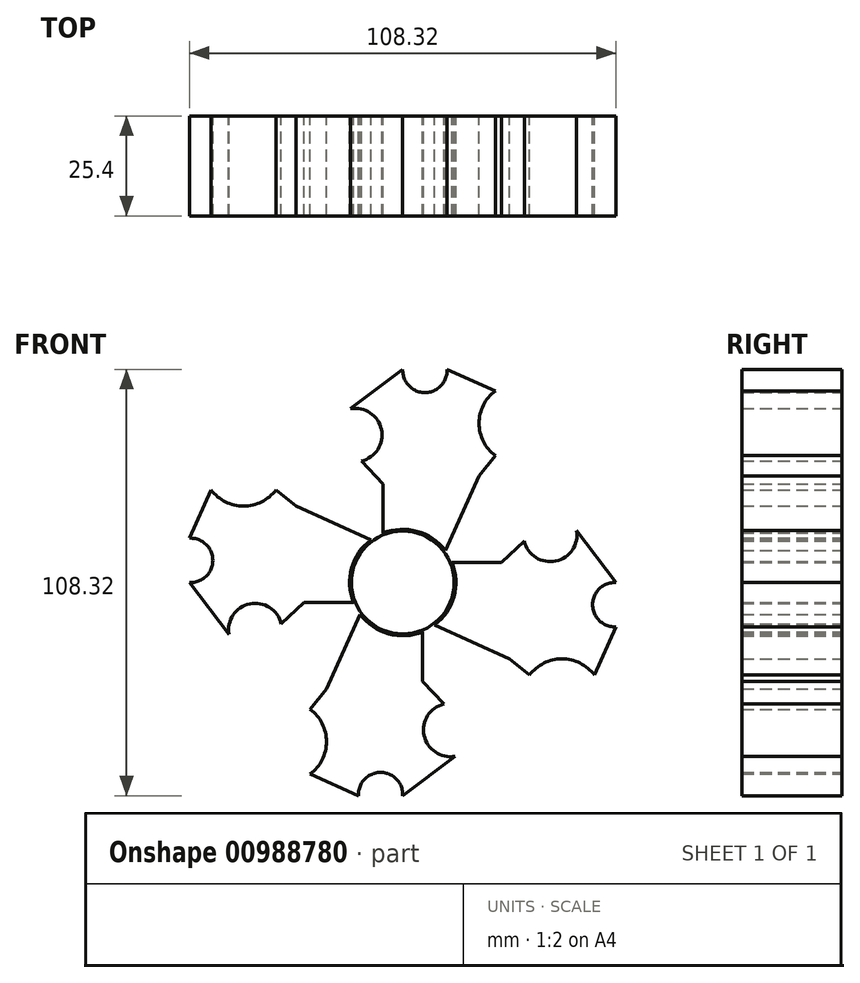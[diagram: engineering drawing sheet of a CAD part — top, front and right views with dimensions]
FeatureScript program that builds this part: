
annotation { "Feature Type Name" : "Feature", "Feature Type Description" : "" }
export const myFeature = defineFeature(function(context is Context, id is Id, definition is map)
    precondition{}
    {
        {
            var Q0;
            Q0=qCreatedBy(makeId("Front.planeOp"),FACE);
            var sketch = newSketch(context, id + "F0", { "sketchPlane" : qUnion([Q0])});
            skCircle(sketch, "E0", {"center": v(0, 0) * mm, "radius": 13.52 * mm});
            skLineSegment(sketch, "E1", {"start": v(12.54, 5.05) * mm, "end": v(25.09, 5.05) * mm});
            skLineSegment(sketch, "E2", {"start": v(25.09, 5.05) * mm, "end": v(30.86, 10.5) * mm});
            skArc(sketch, "E3", {"start": v(30.86, 10.5) * mm, "mid": v(38.85, 5.43) * mm, "end": v(44.16, 13.26) * mm});
            skLineSegment(sketch, "E4", {"start": v(44.16, 13.26) * mm, "end": v(54.16, 0) * mm});
            skArc(sketch, "E5", {"start": v(54.16, 0) * mm, "mid": v(48.25, -5.63) * mm, "end": v(54.16, -11.26) * mm});
            skLineSegment(sketch, "E6", {"start": v(54.16, -11.26) * mm, "end": v(48.67, -23.52) * mm});
            skArc(sketch, "E7", {"start": v(48.67, -23.52) * mm, "mid": v(40.45, -19.4) * mm, "end": v(32.22, -23.52) * mm});
            skLineSegment(sketch, "E8", {"start": v(32.22, -23.52) * mm, "end": v(27.06, -19.4) * mm});
            skPoint(sketch, "E8.endSnap0", {"position": v(40.45, -19.4) * mm});
            skLineSegment(sketch, "E9", {"start": v(27.06, -19.4) * mm, "end": v(8.12, -10.8) * mm});
            skLineSegment(sketch, "E10.1.0", {"start": v(-5.05, 25.09) * mm, "end": v(-10.5, 30.86) * mm});
            skLineSegment(sketch, "E10.1.1", {"start": v(-5.05, 12.54) * mm, "end": v(-5.05, 25.09) * mm});
            skLineSegment(sketch, "E10.1.2", {"start": v(19.4, 27.06) * mm, "end": v(10.8, 8.12) * mm});
            skLineSegment(sketch, "E10.1.3", {"start": v(23.52, 32.22) * mm, "end": v(19.4, 27.06) * mm});
            skArc(sketch, "E10.1.4", {"start": v(23.52, 48.67) * mm, "mid": v(19.4, 40.45) * mm, "end": v(23.52, 32.22) * mm});
            skLineSegment(sketch, "E10.1.5", {"start": v(11.26, 54.16) * mm, "end": v(23.52, 48.67) * mm});
            skArc(sketch, "E10.1.6", {"start": v(0, 54.16) * mm, "mid": v(5.63, 48.25) * mm, "end": v(11.26, 54.16) * mm});
            skLineSegment(sketch, "E10.1.7", {"start": v(-13.26, 44.16) * mm, "end": v(0, 54.16) * mm});
            skArc(sketch, "E10.1.8", {"start": v(-10.5, 30.86) * mm, "mid": v(-5.43, 38.85) * mm, "end": v(-13.26, 44.16) * mm});
            skLineSegment(sketch, "E10.2.0", {"start": v(-25.09, -5.05) * mm, "end": v(-30.86, -10.5) * mm});
            skLineSegment(sketch, "E10.2.1", {"start": v(-12.54, -5.05) * mm, "end": v(-25.09, -5.05) * mm});
            skLineSegment(sketch, "E10.2.2", {"start": v(-27.06, 19.4) * mm, "end": v(-8.12, 10.8) * mm});
            skLineSegment(sketch, "E10.2.3", {"start": v(-32.22, 23.52) * mm, "end": v(-27.06, 19.4) * mm});
            skArc(sketch, "E10.2.4", {"start": v(-48.67, 23.52) * mm, "mid": v(-40.45, 19.4) * mm, "end": v(-32.22, 23.52) * mm});
            skLineSegment(sketch, "E10.2.5", {"start": v(-54.16, 11.26) * mm, "end": v(-48.67, 23.52) * mm});
            skArc(sketch, "E10.2.6", {"start": v(-54.16, 0) * mm, "mid": v(-48.25, 5.63) * mm, "end": v(-54.16, 11.26) * mm});
            skLineSegment(sketch, "E10.2.7", {"start": v(-44.16, -13.26) * mm, "end": v(-54.16, 0) * mm});
            skArc(sketch, "E10.2.8", {"start": v(-30.86, -10.5) * mm, "mid": v(-38.85, -5.43) * mm, "end": v(-44.16, -13.26) * mm});
            skLineSegment(sketch, "E10.3.0", {"start": v(5.05, -25.09) * mm, "end": v(10.5, -30.86) * mm});
            skLineSegment(sketch, "E10.3.1", {"start": v(5.05, -12.54) * mm, "end": v(5.05, -25.09) * mm});
            skLineSegment(sketch, "E10.3.2", {"start": v(-19.4, -27.06) * mm, "end": v(-10.8, -8.12) * mm});
            skLineSegment(sketch, "E10.3.3", {"start": v(-23.52, -32.22) * mm, "end": v(-19.4, -27.06) * mm});
            skArc(sketch, "E10.3.4", {"start": v(-23.52, -48.67) * mm, "mid": v(-19.4, -40.45) * mm, "end": v(-23.52, -32.22) * mm});
            skLineSegment(sketch, "E10.3.5", {"start": v(-11.26, -54.16) * mm, "end": v(-23.52, -48.67) * mm});
            skArc(sketch, "E10.3.6", {"start": v(0, -54.16) * mm, "mid": v(-5.63, -48.25) * mm, "end": v(-11.26, -54.16) * mm});
            skLineSegment(sketch, "E10.3.7", {"start": v(13.26, -44.16) * mm, "end": v(0, -54.16) * mm});
            skArc(sketch, "E10.3.8", {"start": v(10.5, -30.86) * mm, "mid": v(5.43, -38.85) * mm, "end": v(13.26, -44.16) * mm});
            skSolve(sketch);
        }
        {
            var Q0;
            {var subQ0=sQuery(id+"F0.wireOp",EDGE,"E1");Q0=makeQuery(id+"F0.imprint","IMPRINT",FACE,{"disambiguationData":[TD([[makeQuery(id+"F0.imprint","IMPRINT",EDGE,{"derivedFrom":subQ0}),-1.0]])]});}
            var Q1;
            Q1=makeQuery(id+"F0.imprint","IMPRINT",FACE,{"disambiguationData":[TD([[makeQuery(id+"F0.imprint","IMPRINT",EDGE,{"derivedFrom":sQuery(id+"F0.wireOp",EDGE,"E10.1.0")}),-1.0]])]});
            var Q2;
            Q2=makeQuery(id+"F0.imprint","IMPRINT",FACE,{"disambiguationData":[TD([[makeQuery(id+"F0.imprint","IMPRINT",EDGE,{"derivedFrom":sQuery(id+"F0.wireOp",EDGE,"E10.2.0")}),-1.0]])]});
            var Q3;
            Q3=makeQuery(id+"F0.imprint","IMPRINT",FACE,{"disambiguationData":[TD([[makeQuery(id+"F0.imprint","IMPRINT",EDGE,{"derivedFrom":sQuery(id+"F0.wireOp",EDGE,"E10.3.0")}),-1.0]])]});
            extrude(context, id + "F1", {"entities" : qUnion([Q0, Q1, Q2, Q3]), "depth" : 25.4 * mm, "offsetDistance" : 25.4 * mm});
        }
        {
            var Q0;
            Q0=qCreatedBy(makeId("Front.planeOp"),FACE);
            var sketch = newSketch(context, id + "F2", { "sketchPlane" : qUnion([Q0])});
            skCircle(sketch, "E11", {"center": v(0, 0) * mm, "radius": 13.07 * mm});
            skSolve(sketch);
        }
        {
            var Q0;
            Q0=makeQuery(id+"F2.imprint","IMPRINT",FACE,{"disambiguationData":[TD([[makeQuery(id+"F2.imprint","IMPRINT",EDGE,{"derivedFrom":sQuery(id+"F2.wireOp",EDGE,"E11")}),1.0]])]});
            extrude(context, id + "F3", {"entities" : qUnion([Q0]), "depth" : 25.4 * mm, "offsetDistance" : 25.4 * mm});
        }
    });
